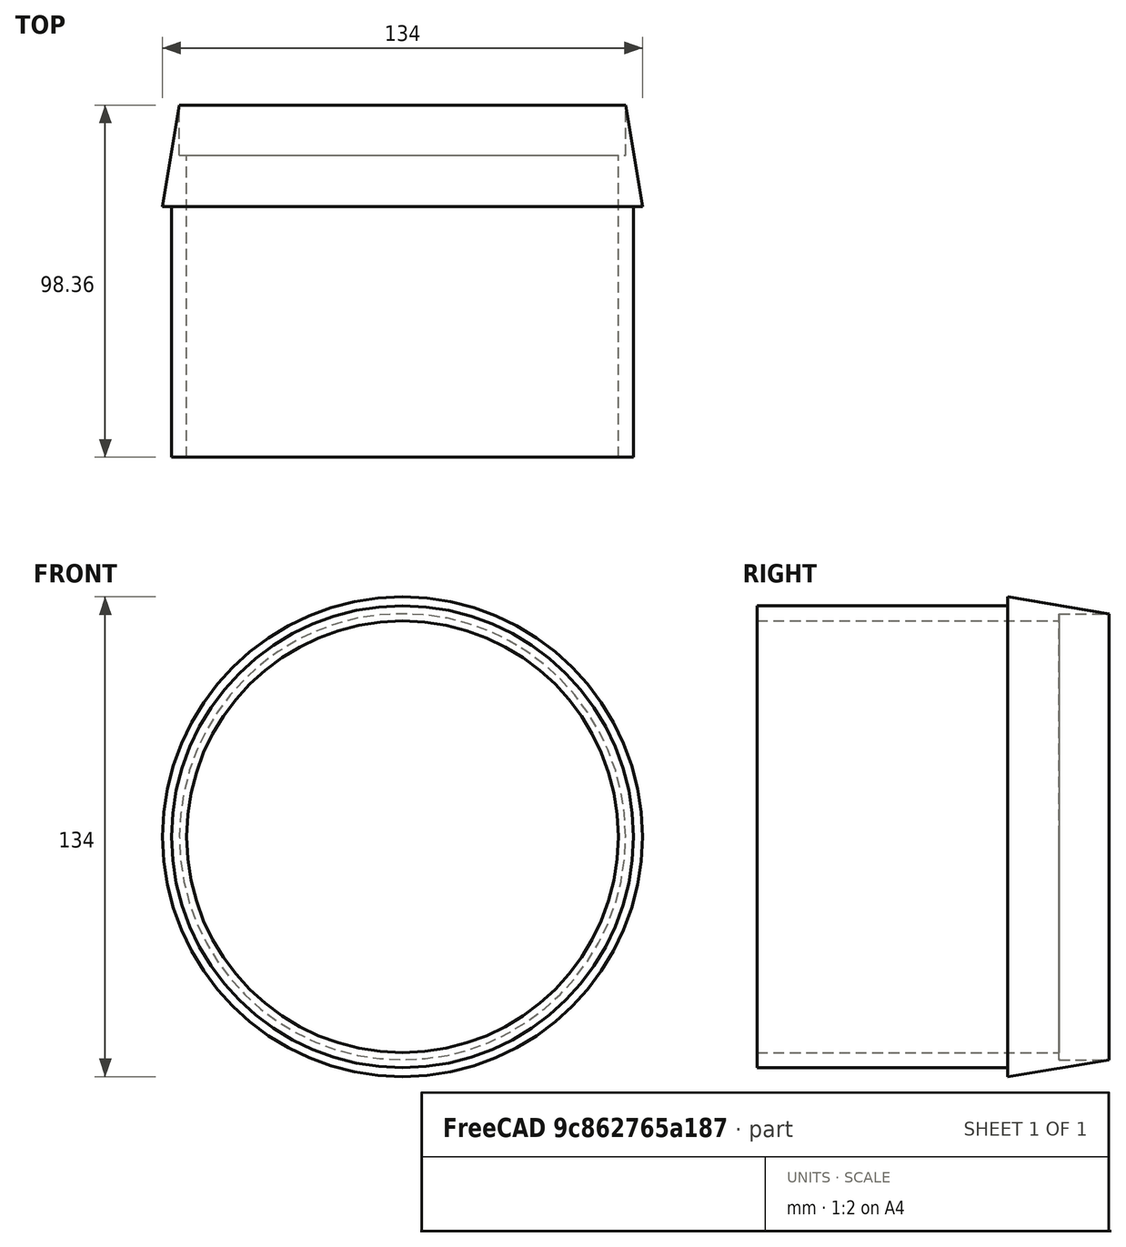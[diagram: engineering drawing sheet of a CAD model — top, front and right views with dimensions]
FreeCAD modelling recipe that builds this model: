
FCSTD DOCUMENT  (FreeCAD 0.19R24291 (Git))
Label: TransitionPiece
License: All rights reserved
LicenseURL: http://en.wikipedia.org/wiki/All_rights_reserved
objects: Sketcher::SketchObject×1, PartDesign::Revolution×1, PartDesign::Body×1, App::Part×1
note: 4 computed .brp shape members not serialized (recipe doc carries the construction recipe); baked Part::Feature solids carry a one-line shape summary decoded from their .brp

FEATURE [Sketcher::SketchObject] Sketch
  FullyConstrained = false
  MapMode = 5
  Support = -> [XY_Plane001]
  sketch-geometry (7):
    g0: LineSegment StartX=-60.3 StartY=31.5235 StartZ=0 EndX=-62.3 EndY=31.5235 EndZ=0
    g1: LineSegment StartX=-62.3 StartY=31.5235 StartZ=0 EndX=-62.3 EndY=45.4796 EndZ=0
    g2: LineSegment StartX=-62.3 StartY=45.4796 StartZ=0 EndX=-67 EndY=17.1196 EndZ=0
    g3: LineSegment StartX=-67 StartY=17.1196 StartZ=0 EndX=-64.5 EndY=17.1196 EndZ=0
    g4: LineSegment StartX=-64.5 StartY=17.1196 StartZ=0 EndX=-64.5 EndY=-52.8804 EndZ=0
    g5: LineSegment StartX=-64.5 StartY=-52.8804 StartZ=0 EndX=-60.3 EndY=-52.8804 EndZ=0
    g6: LineSegment StartX=-60.3 StartY=-52.8804 StartZ=0 EndX=-60.3 EndY=31.5235 EndZ=0
  constraints (19):
    c: Horizontal(g0)
    c: Coincident(g1,g0)
    c: Coincident(g2,g1)
    c: Coincident(g3,g2)
    c: Coincident(g4,g3)
    c: Vertical(g4)
    c: Coincident(g5,g4)
    c: Horizontal(g5)
    c: Coincident(g6,g5)
    c: Coincident(g6,g0)
    c: Vertical(g6)
    c: Vertical(g1)
    c: Horizontal(g3)
    c: DistanceX(g0,g-1) = 62.3
    c: DistanceX(g2,g-1) = 67
    c: DistanceX(g4,g-1) = 64.5
    c: DistanceX(g0,g0) = 2
    c: DistanceY(g3,g1) = 28.36
    c: DistanceY(g4,g4) = 70
FEATURE [PartDesign::Revolution] Revolution
  Angle = 360
  Axis = (0,1,0)
  Base = (0,0,0)
  Profile = -> Sketch
  ReferenceAxis = -> Sketch [V_Axis]
FEATURE [PartDesign::Body] Body
  Group = -> [Sketch,Revolution]
  Origin = -> Origin001
  Tip = -> Revolution
FEATURE [App::Part] Part
  Group = -> [Body]
  Origin = -> Origin
